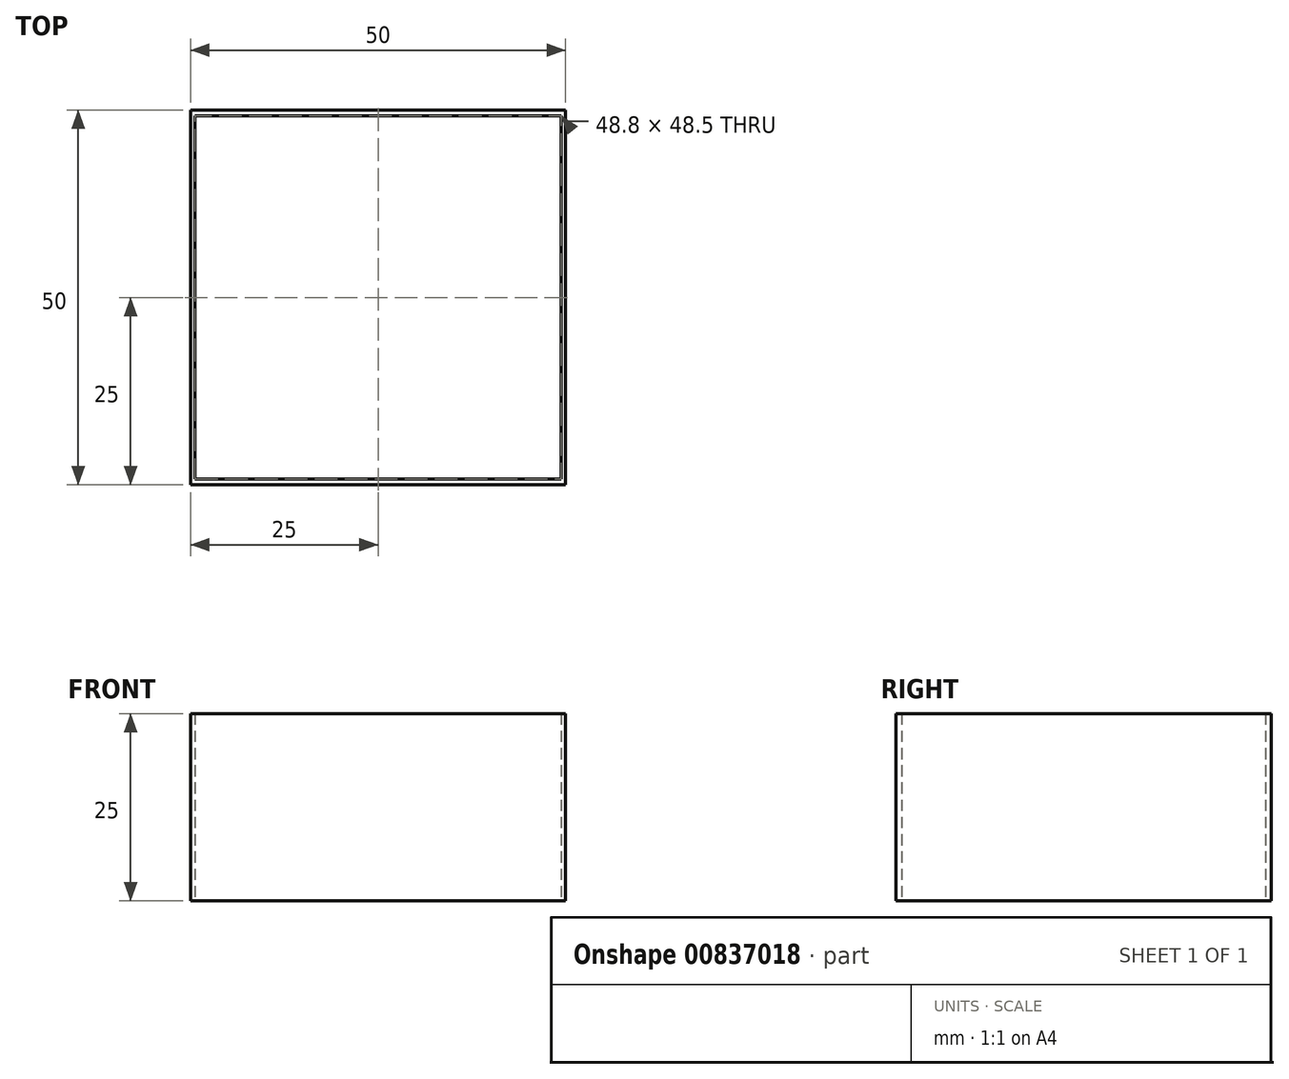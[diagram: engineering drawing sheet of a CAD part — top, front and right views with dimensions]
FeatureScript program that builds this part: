
annotation { "Feature Type Name" : "Feature", "Feature Type Description" : "" }
export const myFeature = defineFeature(function(context is Context, id is Id, definition is map)
    precondition{}
    {
        {
            var Q0;
            Q0=qCreatedBy(makeId("Top.planeOp"),FACE);
            var sketch = newSketch(context, id + "F0", { "sketchPlane" : qUnion([Q0])});
            skLineSegment(sketch, "E0.bottom", {"start": v(25, -25) * mm, "end": v(-25, -25) * mm});
            skLineSegment(sketch, "E0.top", {"start": v(25, 25) * mm, "end": v(-25, 25) * mm});
            skLineSegment(sketch, "E0.left", {"start": v(25, -25) * mm, "end": v(25, 25) * mm});
            skLineSegment(sketch, "E0.right", {"start": v(-25, -25) * mm, "end": v(-25, 25) * mm});
            skPoint(sketch, "E0.middle", {"position": v(0, 0) * mm});
            skLineSegment(sketch, "E1.bottom", {"start": v(24.4, -24.25) * mm, "end": v(-24.4, -24.25) * mm});
            skLineSegment(sketch, "E1.top", {"start": v(24.4, 24.25) * mm, "end": v(-24.4, 24.25) * mm});
            skLineSegment(sketch, "E1.left", {"start": v(24.4, -24.25) * mm, "end": v(24.4, 24.25) * mm});
            skLineSegment(sketch, "E1.right", {"start": v(-24.4, -24.25) * mm, "end": v(-24.4, 24.25) * mm});
            skSolve(sketch);
        }
        {
            var Q0;
            Q0=makeQuery(id+"F0.imprint","IMPRINT",FACE,{"disambiguationData":[TD([[makeQuery(id+"F0.imprint","IMPRINT",EDGE,{"derivedFrom":sQuery(id+"F0.wireOp",EDGE,"E0.bottom")}),-1.0]])]});
            extrude(context, id + "F1", {"entities" : qUnion([Q0]), "depth" : 25 * mm, "offsetDistance" : 25 * mm});
        }
    });
